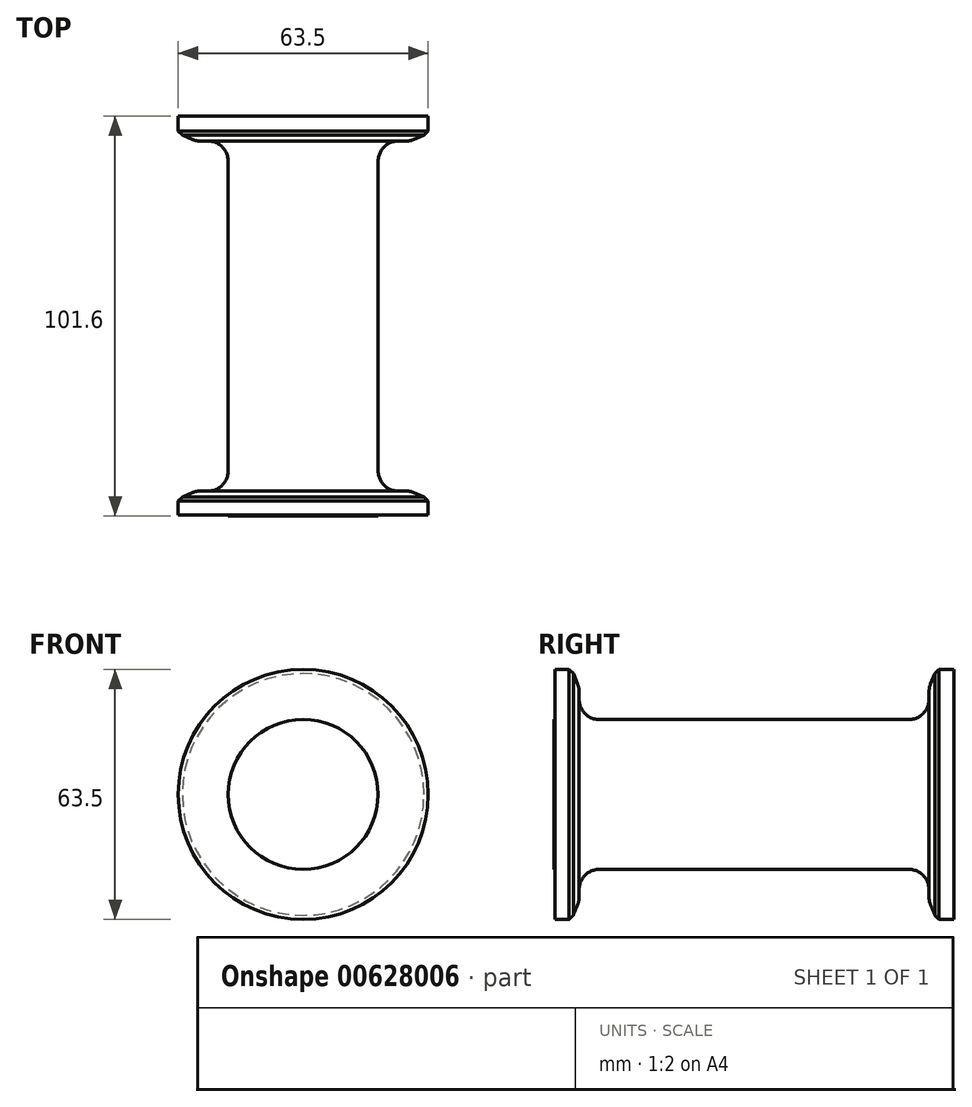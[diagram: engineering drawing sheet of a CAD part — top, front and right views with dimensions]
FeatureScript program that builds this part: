
annotation { "Feature Type Name" : "Feature", "Feature Type Description" : "" }
export const myFeature = defineFeature(function(context is Context, id is Id, definition is map)
    precondition{}
    {
        {
            var Q0;
            Q0=qCreatedBy(makeId("Front.planeOp"),FACE);
            var sketch = newSketch(context, id + "F0", { "sketchPlane" : qUnion([Q0])});
            skCircle(sketch, "E0", {"center": v(0, 0) * mm, "radius": 19.05 * mm});
            skSolve(sketch);
        }
        {
            var Q0;
            Q0=makeQuery(id+"F0.imprint","IMPRINT",FACE,{"disambiguationData":[TD([[makeQuery(id+"F0.imprint","IMPRINT",EDGE,{"derivedFrom":sQuery(id+"F0.wireOp",EDGE,"E0")}),1.0]])]});
            extrude(context, id + "F1", {"entities" : qUnion([Q0]), "depth" : 101.6 * mm, "offsetDistance" : 25.4 * mm});
        }
        {
            var Q0;
            Q0=qCreatedBy(makeId("Front.planeOp"),FACE);
            var sketch = newSketch(context, id + "F2", { "sketchPlane" : qUnion([Q0])});
            skCircle(sketch, "E1", {"center": v(0, 0) * mm, "radius": 31.75 * mm});
            skSolve(sketch);
        }
        {
            var Q0;
            Q0=makeQuery(id+"F2.imprint","IMPRINT",FACE,{"disambiguationData":[TD([[makeQuery(id+"F2.imprint","IMPRINT",EDGE,{"derivedFrom":sQuery(id+"F2.wireOp",EDGE,"E1")}),1.0]])]});
            extrude(context, id + "F3", {"entities" : qUnion([Q0]), "operationType" : NewBodyOperationType.ADD, "depth" : 6.35 * mm, "offsetDistance" : 25.4 * mm});
        }
        {
            var Q0;
            Q0=qCreatedBy(makeId("Front.planeOp"),FACE);
            var sketch = newSketch(context, id + "F4", { "sketchPlane" : qUnion([Q0])});
            skCircle(sketch, "E2", {"center": v(0, 0) * mm, "radius": 31.75 * mm});
            skSolve(sketch);
        }
        {
            var Q0;
            Q0 = qSketchRegion(id + "F4", true);
            extrude(context, id + "F5", {"entities" : qUnion([Q0]), "operationType" : NewBodyOperationType.ADD, "depth" : 101.35 * mm, "offsetDistance" : 25.4 * mm, "hasSecondDirection" : true, "secondDirectionOppositeDirection" : false, "secondDirectionDepth" : 95.25 * mm});
        }
        {
            var Q0;
            Q0=makeQuery(id+"F3.opExtrude","CAP_EDGE",EDGE,{"disambiguationData":[OSD([sQuery(id+"F2.wireOp",EDGE,"E1")])],"isStart":false});
            var Q1;
            Q1=makeQuery(id+"F5.opExtrude","CAP_EDGE",EDGE,{"disambiguationData":[OSD([sQuery(id+"F4.wireOp",EDGE,"E2")])],"isStart":true});
            chamfer(context, id + "F6", {"entities" : qUnion([Q0, Q1]), "width" : 2.54 * mm, "tangentPropagation" : true});
        }
        {
            var Q0;
            {var subQ0=sQuery(id+"F4.wireOp",EDGE,"E2");Q0=makeQuery(id+"F6.opChamfer","BLEND_EDGE",EDGE,{"blendedFrom":[makeQuery(id+"F5.opExtrude","CAP_EDGE",EDGE,{"disambiguationData":[OSD([subQ0])],"isStart":true}),makeQuery(id+"F5.opExtrude","CAP_FACE",FACE,{"disambiguationData":[OSD([subQ0])],"isStart":true})],"blendedInto":[makeQuery(id+"F5.opExtrude","CAP_FACE",FACE,{"disambiguationData":[OSD([subQ0])],"isStart":true})]});}
            var Q1;
            {var subQ0=sQuery(id+"F2.wireOp",EDGE,"E1");Q1=makeQuery(id+"F6.opChamfer","BLEND_EDGE",EDGE,{"blendedFrom":[makeQuery(id+"F3.opExtrude","CAP_EDGE",EDGE,{"disambiguationData":[OSD([subQ0])],"isStart":false}),makeQuery(id+"F3.opExtrude","CAP_FACE",FACE,{"disambiguationData":[OSD([subQ0])],"isStart":false})],"blendedInto":[makeQuery(id+"F3.opExtrude","CAP_FACE",FACE,{"disambiguationData":[OSD([subQ0])],"isStart":false})]});}
            chamfer(context, id + "F7", {"entities" : qUnion([Q0, Q1]), "width" : 5.08 * mm, "tangentPropagation" : true});
        }
        {
            var Q0;
            {var subQ0=sQuery(id+"F2.wireOp",EDGE,"E1");var subQ1=makeQuery(id+"F3.opExtrude","CAP_FACE",FACE,{"disambiguationData":[OSD([subQ0])],"isStart":false});Q0=makeQuery(id+"F7.opChamfer","BLEND_EDGE",EDGE,{"blendedFrom":[makeQuery(id+"F6.opChamfer","BLEND_EDGE",EDGE,{"blendedFrom":[makeQuery(id+"F3.opExtrude","CAP_EDGE",EDGE,{"disambiguationData":[OSD([subQ0])],"isStart":false}),subQ1],"blendedInto":[subQ1]}),subQ1],"blendedInto":[subQ1]});}
            var Q1;
            {var subQ0=sQuery(id+"F4.wireOp",EDGE,"E2");var subQ1=makeQuery(id+"F5.opExtrude","CAP_FACE",FACE,{"disambiguationData":[OSD([subQ0])],"isStart":true});Q1=makeQuery(id+"F7.opChamfer","BLEND_EDGE",EDGE,{"blendedFrom":[makeQuery(id+"F6.opChamfer","BLEND_EDGE",EDGE,{"blendedFrom":[makeQuery(id+"F5.opExtrude","CAP_EDGE",EDGE,{"disambiguationData":[OSD([subQ0])],"isStart":true}),subQ1],"blendedInto":[subQ1]}),subQ1],"blendedInto":[subQ1]});}
            fillet(context, id + "F8", {"entities" : qUnion([Q0, Q1]), "radius" : 5.08 * mm, "tangentPropagation" : true, "allowEdgeOverflow" : false});
        }
        {
            var Q0;
            Q0=makeQuery(id+"F5.boolean.opBoolean","INTERSECT",EDGE,{"derivedFrom":[makeQuery(id+"F1.opExtrude","SWEPT_FACE",FACE,{"disambiguationData":[OSD([sQuery(id+"F0.wireOp",EDGE,"E0")])]}),makeQuery(id+"F5.opExtrude","CAP_FACE",FACE,{"disambiguationData":[OSD([sQuery(id+"F4.wireOp",EDGE,"E2")])],"isStart":true})]});
            var Q1;
            Q1=makeQuery(id+"F3.boolean.opBoolean","INTERSECT",EDGE,{"derivedFrom":[makeQuery(id+"F1.opExtrude","SWEPT_FACE",FACE,{"disambiguationData":[OSD([sQuery(id+"F0.wireOp",EDGE,"E0")])]}),makeQuery(id+"F3.opExtrude","CAP_FACE",FACE,{"disambiguationData":[OSD([sQuery(id+"F2.wireOp",EDGE,"E1")])],"isStart":false})]});
            fillet(context, id + "F9", {"entities" : qUnion([Q0, Q1]), "radius" : 5.08 * mm, "tangentPropagation" : true, "allowEdgeOverflow" : false});
        }
    });
